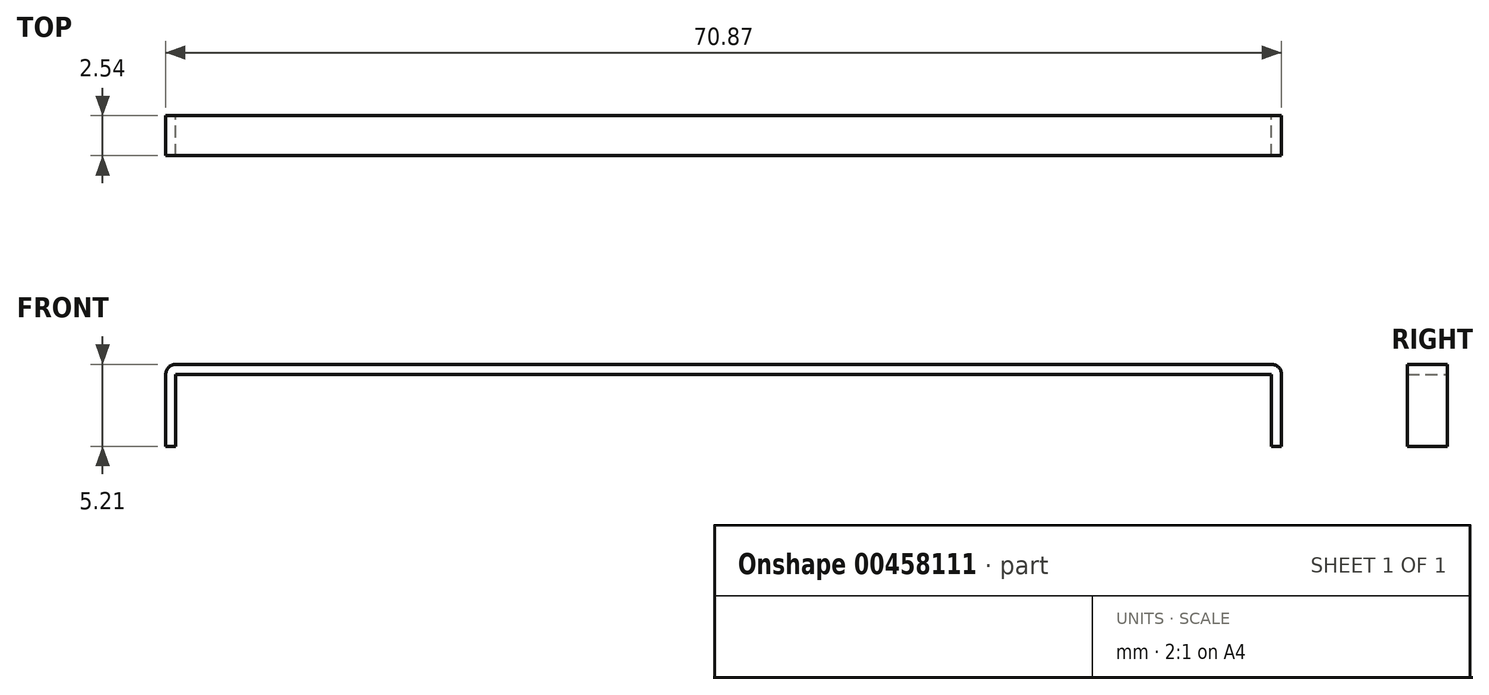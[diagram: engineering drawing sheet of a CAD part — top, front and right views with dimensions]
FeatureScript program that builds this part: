
annotation { "Feature Type Name" : "Feature", "Feature Type Description" : "" }
export const myFeature = defineFeature(function(context is Context, id is Id, definition is map)
    precondition{}
    {
        {
            var Q0;
            Q0=qCreatedBy(makeId("Front.planeOp"),FACE);
            var sketch = newSketch(context, id + "F0", { "sketchPlane" : qUnion([Q0])});
            skLineSegment(sketch, "E0", {"start": v(0, 0) * mm, "end": v(69.6, 0) * mm});
            skLineSegment(sketch, "E1", {"start": v(69.6, 0) * mm, "end": v(69.6, -4.57) * mm});
            skLineSegment(sketch, "E2", {"start": v(69.6, -4.57) * mm, "end": v(70.23, -4.57) * mm});
            skLineSegment(sketch, "E3", {"start": v(70.23, -4.57) * mm, "end": v(70.23, 0) * mm});
            skLineSegment(sketch, "E4", {"start": v(69.6, 0.64) * mm, "end": v(0, 0.63) * mm});
            skLineSegment(sketch, "E5", {"start": v(-0.64, 0) * mm, "end": v(-0.64, -4.57) * mm});
            skLineSegment(sketch, "E6", {"start": v(-0.64, -4.57) * mm, "end": v(0, -4.57) * mm});
            skLineSegment(sketch, "E7", {"start": v(0, -4.57) * mm, "end": v(0, 0) * mm});
            skPoint(sketch, "E8.visualSharp", {"position": v(-0.64, 0.63) * mm});
            skArc(sketch, "E8.filletArc", {"start": v(0, 0.63) * mm, "mid": v(-0.45, 0.45) * mm, "end": v(-0.64, 0) * mm});
            skPoint(sketch, "E9.visualSharp", {"position": v(70.23, 0.64) * mm});
            skArc(sketch, "E9.filletArc", {"start": v(70.23, 0) * mm, "mid": v(70.05, 0.45) * mm, "end": v(69.6, 0.64) * mm});
            skSolve(sketch);
        }
        {
            var Q0;
            Q0=makeQuery(id+"F0.imprint","IMPRINT",FACE,{"disambiguationData":[TD([[makeQuery(id+"F0.imprint","IMPRINT",EDGE,{"derivedFrom":sQuery(id+"F0.wireOp",EDGE,"E0")}),1.0]])]});
            extrude(context, id + "F1", {"entities" : qUnion([Q0]), "endBound" : BoundingType.SYMMETRIC, "depth" : 2.54 * mm});
        }
    });
